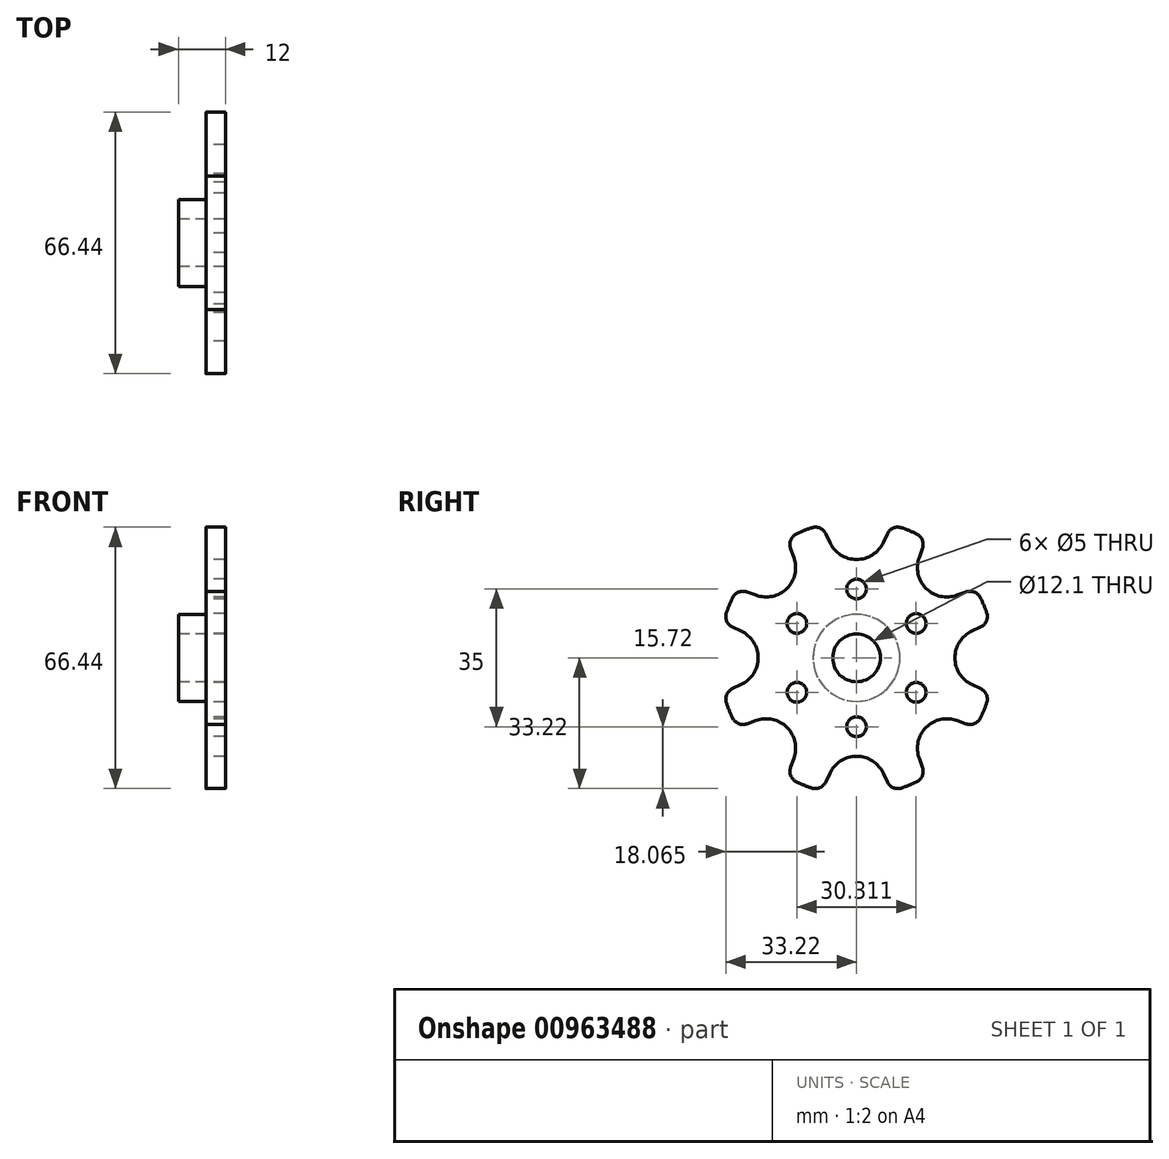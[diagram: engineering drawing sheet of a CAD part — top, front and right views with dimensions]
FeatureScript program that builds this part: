
annotation { "Feature Type Name" : "Feature", "Feature Type Description" : "" }
export const myFeature = defineFeature(function(context is Context, id is Id, definition is map)
    precondition{}
    {
        {
            var Q0;
            Q0=qCreatedBy(makeId("Right.planeOp"),FACE);
            var sketch = newSketch(context, id + "F0", { "sketchPlane" : qUnion([Q0])});
            skCircle(sketch, "E0", {"center": v(0, 0) * mm, "radius": 25 * mm, "construction": true});
            skArc(sketch, "E1", {"start": v(-8.9, 33.85) * mm, "mid": v(0, -35) * mm, "end": v(8.9, 33.85) * mm, "construction": true});
            skLineSegment(sketch, "E2", {"start": v(0, 0) * mm, "end": v(0, 35) * mm, "construction": true});
            skLineSegment(sketch, "E3.1.0", {"start": v(0, 0) * mm, "end": v(-13.4, 32.34) * mm, "construction": true});
            skLineSegment(sketch, "E3.2.0", {"start": v(0, 0) * mm, "end": v(-17.68, 17.68) * mm, "construction": true});
            skLineSegment(sketch, "E3.3.0", {"start": v(0, 0) * mm, "end": v(-23.1, 9.57) * mm, "construction": true});
            skLineSegment(sketch, "E3.4.0", {"start": v(0, 0) * mm, "end": v(-25, 0) * mm, "construction": true});
            skLineSegment(sketch, "E3.5.0", {"start": v(0, 0) * mm, "end": v(-23.1, -9.57) * mm, "construction": true});
            skLineSegment(sketch, "E3.6.0", {"start": v(0, 0) * mm, "end": v(-17.68, -17.68) * mm, "construction": true});
            skLineSegment(sketch, "E3.7.0", {"start": v(0, 0) * mm, "end": v(-9.57, -23.1) * mm, "construction": true});
            skLineSegment(sketch, "E3.8.0", {"start": v(0, 0) * mm, "end": v(0, -25) * mm, "construction": true});
            skLineSegment(sketch, "E3.9.0", {"start": v(0, 0) * mm, "end": v(9.57, -23.1) * mm, "construction": true});
            skLineSegment(sketch, "E3.10.0", {"start": v(0, 0) * mm, "end": v(17.68, -17.68) * mm, "construction": true});
            skLineSegment(sketch, "E3.11.0", {"start": v(0, 0) * mm, "end": v(23.1, -9.57) * mm, "construction": true});
            skLineSegment(sketch, "E3.12.0", {"start": v(0, 0) * mm, "end": v(25, 0) * mm, "construction": true});
            skLineSegment(sketch, "E3.13.0", {"start": v(0, 0) * mm, "end": v(23.1, 9.57) * mm, "construction": true});
            skLineSegment(sketch, "E3.14.0", {"start": v(0, 0) * mm, "end": v(17.68, 17.68) * mm, "construction": true});
            skLineSegment(sketch, "E3.15.0", {"start": v(0, 0) * mm, "end": v(13.4, 32.34) * mm, "construction": true});
            skPoint(sketch, "E4.orphan", {"position": v(0, 25) * mm});
            skPoint(sketch, "E5.orphan", {"position": v(-9.57, 23.1) * mm});
            skPoint(sketch, "E6.orphan", {"position": v(9.57, 23.1) * mm});
            skArc(sketch, "E7", {"start": v(-6.8, 29.33) * mm, "mid": v(0, 25) * mm, "end": v(6.8, 29.33) * mm});
            skLineSegment(sketch, "E8", {"start": v(6.8, 29.33) * mm, "end": v(0, 29.33) * mm, "construction": true});
            skLineSegment(sketch, "E9", {"start": v(-6.8, 29.33) * mm, "end": v(0, 29.33) * mm, "construction": true});
            skLineSegment(sketch, "E10", {"start": v(-6.8, 29.33) * mm, "end": v(-7.8, 31.49) * mm});
            skLineSegment(sketch, "E11", {"start": v(6.8, 29.33) * mm, "end": v(7.8, 31.49) * mm});
            skLineSegment(sketch, "E12.1.0", {"start": v(-15.93, 25.55) * mm, "end": v(-16.75, 27.78) * mm});
            skArc(sketch, "E12.1.1", {"start": v(-25.55, 15.93) * mm, "mid": v(-17.68, 17.68) * mm, "end": v(-15.93, 25.55) * mm});
            skLineSegment(sketch, "E12.1.2", {"start": v(-25.55, 15.93) * mm, "end": v(-27.78, 16.75) * mm});
            skLineSegment(sketch, "E12.2.0", {"start": v(-29.33, 6.8) * mm, "end": v(-31.49, 7.8) * mm});
            skArc(sketch, "E12.2.1", {"start": v(-29.33, -6.8) * mm, "mid": v(-25, 0) * mm, "end": v(-29.33, 6.8) * mm});
            skLineSegment(sketch, "E12.2.2", {"start": v(-29.33, -6.8) * mm, "end": v(-31.49, -7.8) * mm});
            skLineSegment(sketch, "E12.3.0", {"start": v(-25.55, -15.93) * mm, "end": v(-27.78, -16.75) * mm});
            skArc(sketch, "E12.3.1", {"start": v(-15.93, -25.55) * mm, "mid": v(-17.68, -17.68) * mm, "end": v(-25.55, -15.93) * mm});
            skLineSegment(sketch, "E12.3.2", {"start": v(-15.93, -25.55) * mm, "end": v(-16.75, -27.78) * mm});
            skLineSegment(sketch, "E12.4.0", {"start": v(-6.8, -29.33) * mm, "end": v(-7.8, -31.49) * mm});
            skArc(sketch, "E12.4.1", {"start": v(6.8, -29.33) * mm, "mid": v(0, -25) * mm, "end": v(-6.8, -29.33) * mm});
            skLineSegment(sketch, "E12.4.2", {"start": v(6.8, -29.33) * mm, "end": v(7.8, -31.49) * mm});
            skLineSegment(sketch, "E12.5.0", {"start": v(15.93, -25.55) * mm, "end": v(16.75, -27.78) * mm});
            skArc(sketch, "E12.5.1", {"start": v(25.55, -15.93) * mm, "mid": v(17.68, -17.68) * mm, "end": v(15.93, -25.55) * mm});
            skLineSegment(sketch, "E12.5.2", {"start": v(25.55, -15.93) * mm, "end": v(27.78, -16.75) * mm});
            skLineSegment(sketch, "E12.6.0", {"start": v(29.33, -6.8) * mm, "end": v(31.49, -7.8) * mm});
            skArc(sketch, "E12.6.1", {"start": v(29.33, 6.8) * mm, "mid": v(25, 0) * mm, "end": v(29.33, -6.8) * mm});
            skLineSegment(sketch, "E12.6.2", {"start": v(29.33, 6.8) * mm, "end": v(31.49, 7.8) * mm});
            skLineSegment(sketch, "E12.7.0", {"start": v(25.55, 15.93) * mm, "end": v(27.78, 16.75) * mm});
            skArc(sketch, "E12.7.1", {"start": v(15.93, 25.55) * mm, "mid": v(17.68, 17.68) * mm, "end": v(25.55, 15.93) * mm});
            skLineSegment(sketch, "E12.7.2", {"start": v(15.93, 25.55) * mm, "end": v(16.75, 27.78) * mm});
            skArc(sketch, "E13", {"start": v(-11.5, 33.05) * mm, "mid": v(-13.4, 32.34) * mm, "end": v(-15.23, 31.51) * mm});
            skArc(sketch, "E14", {"start": v(15.23, 31.51) * mm, "mid": v(13.4, 32.34) * mm, "end": v(11.5, 33.05) * mm});
            skLineSegment(sketch, "E15.2.0", {"start": v(0, 0) * mm, "end": v(-24.75, 24.75) * mm, "construction": true});
            skLineSegment(sketch, "E15.3.0", {"start": v(0, 0) * mm, "end": v(-32.34, 13.4) * mm, "construction": true});
            skLineSegment(sketch, "E15.4.0", {"start": v(0, 0) * mm, "end": v(-35, 0) * mm, "construction": true});
            skLineSegment(sketch, "E15.5.0", {"start": v(0, 0) * mm, "end": v(-32.34, -13.4) * mm, "construction": true});
            skLineSegment(sketch, "E15.6.0", {"start": v(0, 0) * mm, "end": v(-24.75, -24.75) * mm, "construction": true});
            skLineSegment(sketch, "E15.7.0", {"start": v(0, 0) * mm, "end": v(-13.4, -32.34) * mm, "construction": true});
            skLineSegment(sketch, "E16.1.8.0", {"start": v(0, 0) * mm, "end": v(0, -35) * mm, "construction": true});
            skLineSegment(sketch, "E16.1.9.0", {"start": v(0, 0) * mm, "end": v(13.4, -32.34) * mm, "construction": true});
            skLineSegment(sketch, "E16.1.10.0", {"start": v(0, 0) * mm, "end": v(24.75, -24.75) * mm, "construction": true});
            skLineSegment(sketch, "E16.1.11.0", {"start": v(0, 0) * mm, "end": v(32.34, -13.4) * mm, "construction": true});
            skLineSegment(sketch, "E16.1.12.0", {"start": v(0, 0) * mm, "end": v(35, 0) * mm, "construction": true});
            skLineSegment(sketch, "E16.1.13.0", {"start": v(0, 0) * mm, "end": v(32.34, 13.4) * mm, "construction": true});
            skLineSegment(sketch, "E16.1.14.0", {"start": v(0, 0) * mm, "end": v(24.75, 24.75) * mm, "construction": true});
            skArc(sketch, "E17", {"start": v(33.05, 11.5) * mm, "mid": v(32.34, 13.4) * mm, "end": v(31.51, 15.23) * mm});
            skArc(sketch, "E18", {"start": v(31.51, -15.23) * mm, "mid": v(32.34, -13.4) * mm, "end": v(33.05, -11.5) * mm});
            skArc(sketch, "E19", {"start": v(11.5, -33.05) * mm, "mid": v(13.4, -32.34) * mm, "end": v(15.23, -31.51) * mm});
            skArc(sketch, "E20", {"start": v(-15.23, -31.51) * mm, "mid": v(-13.4, -32.34) * mm, "end": v(-11.5, -33.05) * mm});
            skArc(sketch, "E21", {"start": v(-33.05, -11.5) * mm, "mid": v(-32.34, -13.4) * mm, "end": v(-31.51, -15.23) * mm});
            skArc(sketch, "E22", {"start": v(-31.51, 15.23) * mm, "mid": v(-32.34, 13.4) * mm, "end": v(-33.05, 11.5) * mm});
            skPoint(sketch, "E23.visualSharp", {"position": v(-8.9, 33.85) * mm});
            skArc(sketch, "E23.filletArc", {"start": v(-7.8, 31.49) * mm, "mid": v(-9.36, 32.98) * mm, "end": v(-11.5, 33.05) * mm});
            skPoint(sketch, "E24.visualSharp", {"position": v(8.9, 33.85) * mm});
            skArc(sketch, "E24.filletArc", {"start": v(11.5, 33.05) * mm, "mid": v(9.36, 32.98) * mm, "end": v(7.8, 31.49) * mm});
            skPoint(sketch, "E25.visualSharp", {"position": v(17.64, 30.23) * mm});
            skArc(sketch, "E25.filletArc", {"start": v(16.75, 27.78) * mm, "mid": v(16.7, 29.94) * mm, "end": v(15.23, 31.51) * mm});
            skPoint(sketch, "E26.visualSharp", {"position": v(30.23, 17.64) * mm});
            skArc(sketch, "E26.filletArc", {"start": v(31.51, 15.23) * mm, "mid": v(29.94, 16.7) * mm, "end": v(27.78, 16.75) * mm});
            skPoint(sketch, "E27.visualSharp", {"position": v(33.85, 8.9) * mm});
            skArc(sketch, "E27.filletArc", {"start": v(31.49, 7.8) * mm, "mid": v(32.98, 9.36) * mm, "end": v(33.05, 11.5) * mm});
            skPoint(sketch, "E28.visualSharp", {"position": v(33.85, -8.9) * mm});
            skArc(sketch, "E28.filletArc", {"start": v(33.05, -11.5) * mm, "mid": v(32.98, -9.36) * mm, "end": v(31.49, -7.8) * mm});
            skPoint(sketch, "E29.visualSharp", {"position": v(30.23, -17.64) * mm});
            skArc(sketch, "E29.filletArc", {"start": v(27.78, -16.75) * mm, "mid": v(29.94, -16.7) * mm, "end": v(31.51, -15.23) * mm});
            skPoint(sketch, "E30.visualSharp", {"position": v(17.64, -30.23) * mm});
            skArc(sketch, "E30.filletArc", {"start": v(15.23, -31.51) * mm, "mid": v(16.7, -29.94) * mm, "end": v(16.75, -27.78) * mm});
            skPoint(sketch, "E31.visualSharp", {"position": v(8.9, -33.85) * mm});
            skArc(sketch, "E31.filletArc", {"start": v(7.8, -31.49) * mm, "mid": v(9.36, -32.98) * mm, "end": v(11.5, -33.05) * mm});
            skPoint(sketch, "E32.visualSharp", {"position": v(-8.9, -33.85) * mm});
            skArc(sketch, "E32.filletArc", {"start": v(-11.5, -33.05) * mm, "mid": v(-9.36, -32.98) * mm, "end": v(-7.8, -31.49) * mm});
            skPoint(sketch, "E33.visualSharp", {"position": v(-17.64, -30.23) * mm});
            skArc(sketch, "E33.filletArc", {"start": v(-16.75, -27.78) * mm, "mid": v(-16.7, -29.94) * mm, "end": v(-15.23, -31.51) * mm});
            skPoint(sketch, "E34.visualSharp", {"position": v(-30.23, -17.64) * mm});
            skArc(sketch, "E34.filletArc", {"start": v(-31.51, -15.23) * mm, "mid": v(-29.94, -16.7) * mm, "end": v(-27.78, -16.75) * mm});
            skPoint(sketch, "E35.visualSharp", {"position": v(-33.85, -8.9) * mm});
            skArc(sketch, "E35.filletArc", {"start": v(-31.49, -7.8) * mm, "mid": v(-32.98, -9.36) * mm, "end": v(-33.05, -11.5) * mm});
            skPoint(sketch, "E36.visualSharp", {"position": v(-33.85, 8.9) * mm});
            skArc(sketch, "E36.filletArc", {"start": v(-33.05, 11.5) * mm, "mid": v(-32.98, 9.36) * mm, "end": v(-31.49, 7.8) * mm});
            skPoint(sketch, "E37.visualSharp", {"position": v(-30.23, 17.64) * mm});
            skArc(sketch, "E37.filletArc", {"start": v(-27.78, 16.75) * mm, "mid": v(-29.94, 16.7) * mm, "end": v(-31.51, 15.23) * mm});
            skPoint(sketch, "E38.visualSharp", {"position": v(-17.64, 30.23) * mm});
            skArc(sketch, "E38.filletArc", {"start": v(-15.23, 31.51) * mm, "mid": v(-16.7, 29.94) * mm, "end": v(-16.75, 27.78) * mm});
            skCircle(sketch, "E39", {"center": v(0, 0) * mm, "radius": 6.05 * mm});
            skCircle(sketch, "E40", {"center": v(0, 17.5) * mm, "radius": 2.5 * mm});
            skCircle(sketch, "E41.1.0", {"center": v(-15.16, 8.75) * mm, "radius": 2.5 * mm});
            skCircle(sketch, "E41.2.0", {"center": v(-15.16, -8.75) * mm, "radius": 2.5 * mm});
            skCircle(sketch, "E41.3.0", {"center": v(0, -17.5) * mm, "radius": 2.5 * mm});
            skCircle(sketch, "E41.4.0", {"center": v(15.16, -8.75) * mm, "radius": 2.5 * mm});
            skCircle(sketch, "E41.5.0", {"center": v(15.16, 8.75) * mm, "radius": 2.5 * mm});
            skSolve(sketch);
        }
        {
            var Q0;
            Q0=qSketchRegion(id+"F0",true);
            extrude(context, id + "F1", {"entities" : qUnion([Q0]), "depth" : 5 * mm});
        }
        {
            var Q0;
            Q0=qCreatedBy(makeId("Front.planeOp"),FACE);
            var sketch = newSketch(context, id + "F2", { "sketchPlane" : qUnion([Q0])});
            skLineSegment(sketch, "E42", {"start": v(0, 6.05) * mm, "end": v(0, 11.05) * mm});
            skLineSegment(sketch, "E43", {"start": v(0, 11.05) * mm, "end": v(-7, 11.05) * mm});
            skLineSegment(sketch, "E44", {"start": v(-7, 11.05) * mm, "end": v(-7, 6.05) * mm});
            skLineSegment(sketch, "E45", {"start": v(-7, 6.05) * mm, "end": v(0, 6.05) * mm});
            skLineSegment(sketch, "E46", {"start": v(-19.9, 0) * mm, "end": v(39.42, 0) * mm, "construction": true});
            skSolve(sketch);
        }
        {
            var Q0;
            Q0=qSketchRegion(id+"F2",true);
            var Q1;
            Q1=sQuery(id+"F2.wireOp",EDGE,"E46");
            revolve(context, id + "F3", {"operationType" : NewBodyOperationType.ADD, "entities" : qUnion([Q0]), "axis" : qUnion([Q1]), "revolveType" : RevolveType.FULL});
        }
    });
